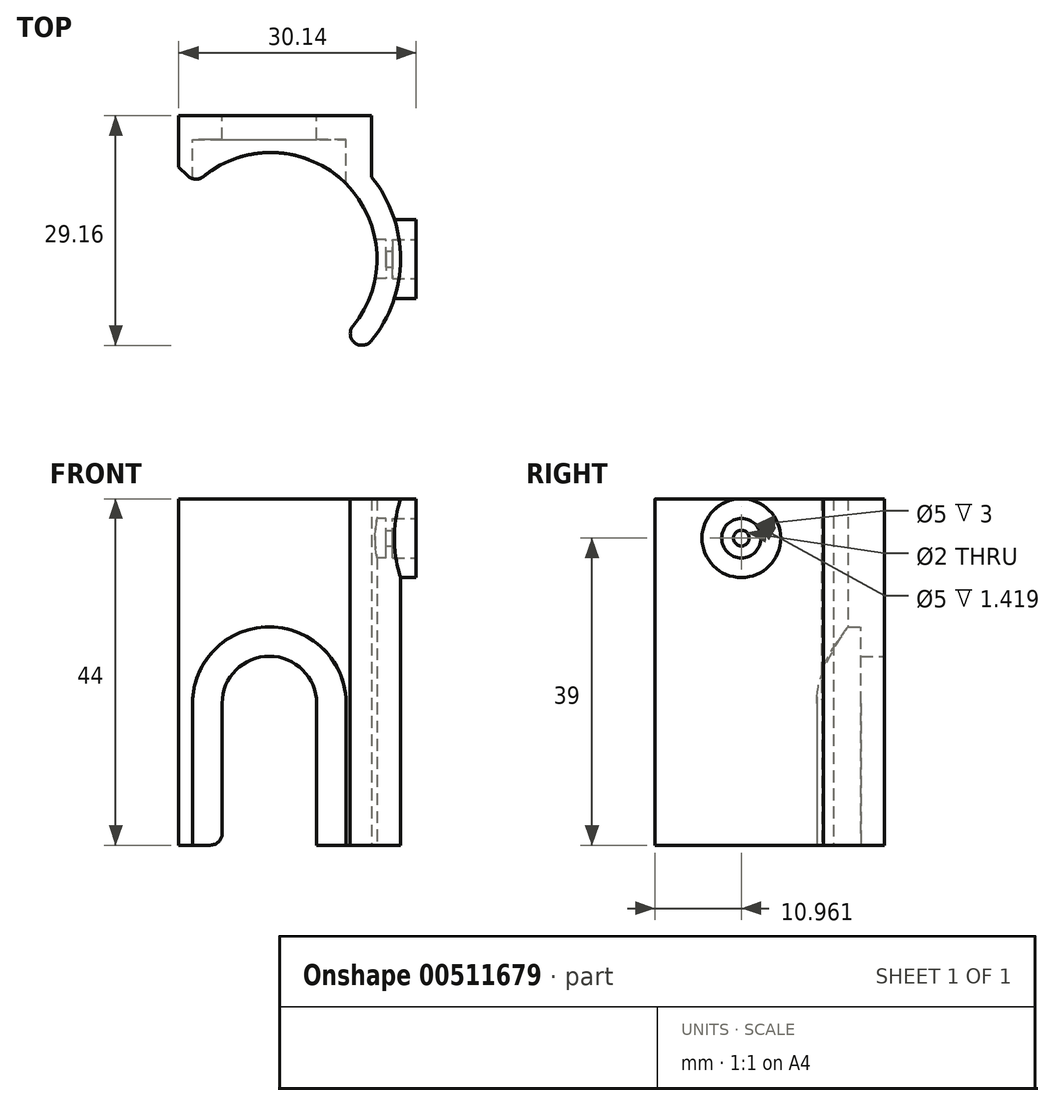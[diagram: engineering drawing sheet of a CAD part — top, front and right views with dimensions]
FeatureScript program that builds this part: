
annotation { "Feature Type Name" : "Feature", "Feature Type Description" : "" }
export const myFeature = defineFeature(function(context is Context, id is Id, definition is map)
    precondition{}
    {
        {
            var Q0;
            Q0=qCreatedBy(makeId("Top.planeOp"),FACE);
            var sketch = newSketch(context, id + "F0", { "sketchPlane" : qUnion([Q0])});
            skLineSegment(sketch, "E0.bottom", {"start": v(-15.55, 14.81) * mm, "end": v(8.95, 14.81) * mm});
            skLineSegment(sketch, "E0.left", {"start": v(-15.55, 14.81) * mm, "end": v(-15.55, 8.31) * mm});
            skLineSegment(sketch, "E0.right", {"start": v(8.95, 14.81) * mm, "end": v(8.95, 7.02) * mm});
            skArc(sketch, "E1", {"start": v(5.66, -12.9) * mm, "mid": v(5.66, 6.2) * mm, "end": v(-13.43, 6.2) * mm});
            skArc(sketch, "E2.0", {"start": v(7.78, -15.02) * mm, "mid": v(12.6, -4.23) * mm, "end": v(8.95, 7.02) * mm});
            skLineSegment(sketch, "E3", {"start": v(5.66, -12.9) * mm, "end": v(7.78, -15.02) * mm});
            skLineSegment(sketch, "E4", {"start": v(-13.43, 6.2) * mm, "end": v(-15.55, 8.31) * mm});
            skLineSegment(sketch, "E5", {"start": v(-3.88, -3.36) * mm, "end": v(4.91, -3.36) * mm, "construction": true});
            skSolve(sketch);
        }
        {
            var Q0;
            Q0=makeQuery(id+"F0.imprint","IMPRINT",FACE,{"disambiguationData":[TD([[makeQuery(id+"F0.imprint","IMPRINT",EDGE,{"derivedFrom":sQuery(id+"F0.wireOp",EDGE,"E0.bottom")}),-1.0]])]});
            extrude(context, id + "F1", {"entities" : qUnion([Q0]), "endBound" : BoundingType.SYMMETRIC, "depth" : 44 * mm, "offsetDistance" : 25 * mm});
        }
        {
            var Q0;
            Q0=makeQuery(id+"F1.opExtrude","SWEPT_FACE",FACE,{"disambiguationData":[OSD([sQuery(id+"F0.wireOp",EDGE,"E0.bottom")])]});
            var sketch = newSketch(context, id + "F2", { "sketchPlane" : qUnion([Q0])});
            skArc(sketch, "E6", {"start": v(10.05, -4) * mm, "mid": v(4.05, 2) * mm, "end": v(-1.95, -4) * mm});
            skLineSegment(sketch, "E7", {"start": v(10.05, -4) * mm, "end": v(10.05, -22) * mm});
            skLineSegment(sketch, "E8", {"start": v(10.05, -22) * mm, "end": v(-1.95, -22) * mm});
            skLineSegment(sketch, "E9", {"start": v(-1.95, -22) * mm, "end": v(-1.95, -4) * mm});
            skLineSegment(sketch, "E10", {"start": v(4.05, -4) * mm, "end": v(10.05, -4) * mm, "construction": true});
            skSolve(sketch);
        }
        {
            var Q0;
            Q0=makeQuery(id+"F2.imprint","IMPRINT",FACE,{"disambiguationData":[TD([[makeQuery(id+"F2.imprint","IMPRINT",EDGE,{"derivedFrom":sQuery(id+"F2.wireOp",EDGE,"E6")}),1.0]])]});
            extrude(context, id + "F3", {"entities" : qUnion([Q0]), "operationType" : NewBodyOperationType.REMOVE, "endBound" : BoundingType.UP_TO_NEXT, "oppositeDirection" : true, "depth" : 25 * mm, "offsetDistance" : 25 * mm});
        }
        {
            var Q0;
            Q0=makeQuery(id+"F1.opExtrude","SWEPT_FACE",FACE,{"disambiguationData":[OSD([sQuery(id+"F0.wireOp",EDGE,"E0.bottom")])]});
            cPlane(context, id + "F4", {"entities" : qUnion([Q0]), "cplaneType" : CPlaneType.OFFSET, "offset" : 3 * mm, "oppositeDirection" : true, "width" : 150 * mm, "height" : 150 * mm});
        }
        {
            var Q0;
            Q0=qCreatedBy(id+"F4.planeOp",FACE);
            var sketch = newSketch(context, id + "F5", { "sketchPlane" : qUnion([Q0])});
            skLineSegment(sketch, "E11.0.0", {"start": v(-8.95, -22) * mm, "end": v(-1.95, -22) * mm, "construction": true});
            skLineSegment(sketch, "E11.0.1", {"start": v(-1.95, -22) * mm, "end": v(-1.95, -4) * mm, "construction": true});
            skArc(sketch, "E11.0.2", {"start": v(-1.95, -4) * mm, "mid": v(4.05, 2) * mm, "end": v(10.05, -4) * mm, "construction": true});
            skLineSegment(sketch, "E11.0.3", {"start": v(10.05, -4) * mm, "end": v(10.05, -22) * mm, "construction": true});
            skLineSegment(sketch, "E11.0.4", {"start": v(10.05, -22) * mm, "end": v(15.55, -22) * mm, "construction": true});
            skLineSegment(sketch, "E11.0.5", {"start": v(15.55, -22) * mm, "end": v(15.55, 22) * mm, "construction": true});
            skLineSegment(sketch, "E11.0.6", {"start": v(15.55, 22) * mm, "end": v(-8.95, 22) * mm, "construction": true});
            skLineSegment(sketch, "E11.0.7", {"start": v(-8.95, 22) * mm, "end": v(-8.95, -22) * mm, "construction": true});
            skArc(sketch, "E12", {"start": v(13.8, -4) * mm, "mid": v(4.05, 5.75) * mm, "end": v(-5.7, -4) * mm});
            skLineSegment(sketch, "E13", {"start": v(4.05, -4) * mm, "end": v(13.8, -4) * mm, "construction": true});
            skLineSegment(sketch, "E14", {"start": v(13.8, -4) * mm, "end": v(13.8, -22) * mm});
            skLineSegment(sketch, "E15", {"start": v(4.05, -4) * mm, "end": v(-5.7, -4) * mm, "construction": true});
            skLineSegment(sketch, "E16", {"start": v(-5.7, -4) * mm, "end": v(-5.7, -22) * mm});
            skLineSegment(sketch, "E17", {"start": v(-5.7, -22) * mm, "end": v(13.8, -22) * mm});
            skSolve(sketch);
        }
        {
            var Q0;
            Q0=makeQuery(id+"F5.imprint","IMPRINT",FACE,{"disambiguationData":[TD([[makeQuery(id+"F5.imprint","IMPRINT",EDGE,{"derivedFrom":sQuery(id+"F5.wireOp",EDGE,"E12")}),1.0]])]});
            var Q1;
            Q1=makeQuery(id+"F1.opExtrude","CAP_VERTEX",VERTEX,{"disambiguationData":[OSD([sQuery(id+"F0.wireOp",EDGE,"E1"),sQuery(id+"F0.wireOp",EDGE,"E4")])],"isStart":false});
            extrude(context, id + "F6", {"entities" : qUnion([Q0]), "operationType" : NewBodyOperationType.REMOVE, "endBound" : BoundingType.UP_TO_VERTEX, "oppositeDirection" : true, "depth" : 25 * mm, "endBoundEntityVertex" : qUnion([Q1]), "offsetDistance" : 25 * mm});
        }
        {
            var Q0;
            Q0=makeQuery(id+"F1.opExtrude","CAP_EDGE",EDGE,{"disambiguationData":[OSD([sQuery(id+"F0.wireOp",EDGE,"E2.0")])],"isStart":false});
            cPoint(context, id + "F7", {"entities" : qUnion([Q0]), "parameter" : 0.5});
        }
        {
            var Q0;
            Q0=qCreatedBy(makeId("Right.planeOp"),FACE);
            var Q1;
            Q1=qCreatedBy(id+"F7",VERTEX);
            cPlane(context, id + "F8", {"entities" : qUnion([Q0, Q1]), "cplaneType" : CPlaneType.PLANE_POINT, "offset" : 25 * mm, "width" : 150 * mm, "height" : 150 * mm});
        }
        {
            var Q0;
            Q0=qCreatedBy(id+"F8.planeOp",FACE);
            var sketch = newSketch(context, id + "F9", { "sketchPlane" : qUnion([Q0])});
            skCircle(sketch, "E18", {"center": v(-3.39, 17) * mm, "radius": 5 * mm});
            skSolve(sketch);
        }
        {
            var Q0;
            Q0=makeQuery(id+"F9.imprint","IMPRINT",FACE,{"disambiguationData":[TD([[makeQuery(id+"F9.imprint","IMPRINT",EDGE,{"derivedFrom":sQuery(id+"F9.wireOp",EDGE,"E18")}),1.0]])]});
            extrude(context, id + "F10", {"entities" : qUnion([Q0]), "operationType" : NewBodyOperationType.ADD, "endBound" : BoundingType.SYMMETRIC, "oppositeDirection" : true, "depth" : 4 * mm, "offsetDistance" : 25 * mm});
        }
        {
            var Q0;
            Q0=makeQuery(id+"F10.opExtrude","CAP_FACE",FACE,{"disambiguationData":[OSD([sQuery(id+"F9.wireOp",EDGE,"E18")])],"isStart":true});
            var sketch = newSketch(context, id + "F11", { "sketchPlane" : qUnion([Q0])});
            skCircle(sketch, "E19", {"center": v(-3.39, 17) * mm, "radius": 2.5 * mm});
            skSolve(sketch);
        }
        {
            var Q0;
            Q0=makeQuery(id+"F11.imprint","IMPRINT",FACE,{"disambiguationData":[TD([[makeQuery(id+"F11.imprint","IMPRINT",EDGE,{"derivedFrom":sQuery(id+"F11.wireOp",EDGE,"E19")}),1.0]])]});
            extrude(context, id + "F12", {"entities" : qUnion([Q0]), "operationType" : NewBodyOperationType.REMOVE, "oppositeDirection" : true, "depth" : 3 * mm, "offsetDistance" : 25 * mm});
        }
        {
            var Q0;
            Q0=makeQuery(id+"F12.boolean.opBoolean","COPY",FACE,{"derivedFrom":makeQuery(id+"F12.opExtrude","CAP_FACE",FACE,{"disambiguationData":[OSD([sQuery(id+"F11.wireOp",EDGE,"E19")])],"isStart":false})});
            var sketch = newSketch(context, id + "F13", { "sketchPlane" : qUnion([Q0])});
            skCircle(sketch, "E20", {"center": v(-3.39, 17) * mm, "radius": 1 * mm});
            skSolve(sketch);
        }
        {
            var Q0;
            Q0=makeQuery(id+"F13.imprint","IMPRINT",FACE,{"disambiguationData":[TD([[makeQuery(id+"F13.imprint","IMPRINT",EDGE,{"derivedFrom":sQuery(id+"F13.wireOp",EDGE,"E20")}),1.0]])]});
            extrude(context, id + "F14", {"entities" : qUnion([Q0]), "operationType" : NewBodyOperationType.REMOVE, "endBound" : BoundingType.THROUGH_ALL, "oppositeDirection" : true, "depth" : 25 * mm, "offsetDistance" : 25 * mm});
        }
        {
            var Q0;
            Q0=qCreatedBy(makeId("Right.planeOp"),FACE);
            var sketch = newSketch(context, id + "F15", { "sketchPlane" : qUnion([Q0])});
            skCircle(sketch, "E21.0", {"center": v(-3.39, 17) * mm, "radius": 2.5 * mm});
            skSolve(sketch);
        }
        {
            var Q0;
            Q0=makeQuery(id+"F15.imprint","IMPRINT",FACE,{"disambiguationData":[TD([[makeQuery(id+"F15.imprint","IMPRINT",EDGE,{"derivedFrom":sQuery(id+"F15.wireOp",EDGE,"E21.0")}),1.0]])]});
            var Q1;
            Q1=sQuery(id+"F15.wireOp",EDGE,"E21.0");
            var Q2;
            Q2=makeQuery(id+"F12.boolean.opBoolean","COPY",FACE,{"derivedFrom":makeQuery(id+"F12.opExtrude","CAP_FACE",FACE,{"disambiguationData":[OSD([sQuery(id+"F11.wireOp",EDGE,"E19")])],"isStart":false})});
            extrude(context, id + "F16", {"entities" : qUnion([Q0]), "operationType" : NewBodyOperationType.REMOVE, "surfaceEntities" : qUnion([Q1]), "endBound" : BoundingType.UP_TO_SURFACE, "depth" : 10.6 * mm, "endBoundEntityFace" : qUnion([Q2]), "hasOffset" : true, "offsetDistance" : 0.8 * mm});
        }
        {
            var Q0;
            Q0=makeQuery(id+"F1.opExtrude","SWEPT_EDGE",EDGE,{"disambiguationData":[OSD([sQuery(id+"F0.wireOp",EDGE,"E2.0"),sQuery(id+"F0.wireOp",EDGE,"E3")])]});
            var Q1;
            Q1=makeQuery(id+"F1.opExtrude","SWEPT_EDGE",EDGE,{"disambiguationData":[OSD([sQuery(id+"F0.wireOp",EDGE,"E1"),sQuery(id+"F0.wireOp",EDGE,"E4")])]});
            var Q2;
            Q2=makeQuery(id+"F1.opExtrude","SWEPT_EDGE",EDGE,{"disambiguationData":[OSD([sQuery(id+"F0.wireOp",EDGE,"E1"),sQuery(id+"F0.wireOp",EDGE,"E3")])]});
            var Q3;
            Q3=makeQuery(id+"F3.boolean.opBoolean","COPY",EDGE,{"derivedFrom":makeQuery(id+"F3.opExtrude","SWEPT_EDGE",EDGE,{"disambiguationData":[OSD([sQuery(id+"F0.wireOp",EDGE,"E0.bottom"),sQuery(id+"F2.wireOp",EDGE,"E8"),sQuery(id+"F2.wireOp",EDGE,"E9")])]})});
            var Q4;
            Q4=makeQuery(id+"F3.boolean.opBoolean","COPY",EDGE,{"derivedFrom":makeQuery(id+"F3.opExtrude","SWEPT_EDGE",EDGE,{"disambiguationData":[OSD([sQuery(id+"F0.wireOp",EDGE,"E0.bottom"),sQuery(id+"F2.wireOp",EDGE,"E7"),sQuery(id+"F2.wireOp",EDGE,"E8")])]})});
            fillet(context, id + "F17", {"entities" : qUnion([Q0, Q1, Q2, Q3, Q4]), "radius" : 1.5 * mm, "tangentPropagation" : true, "allowEdgeOverflow" : false});
        }
    });
